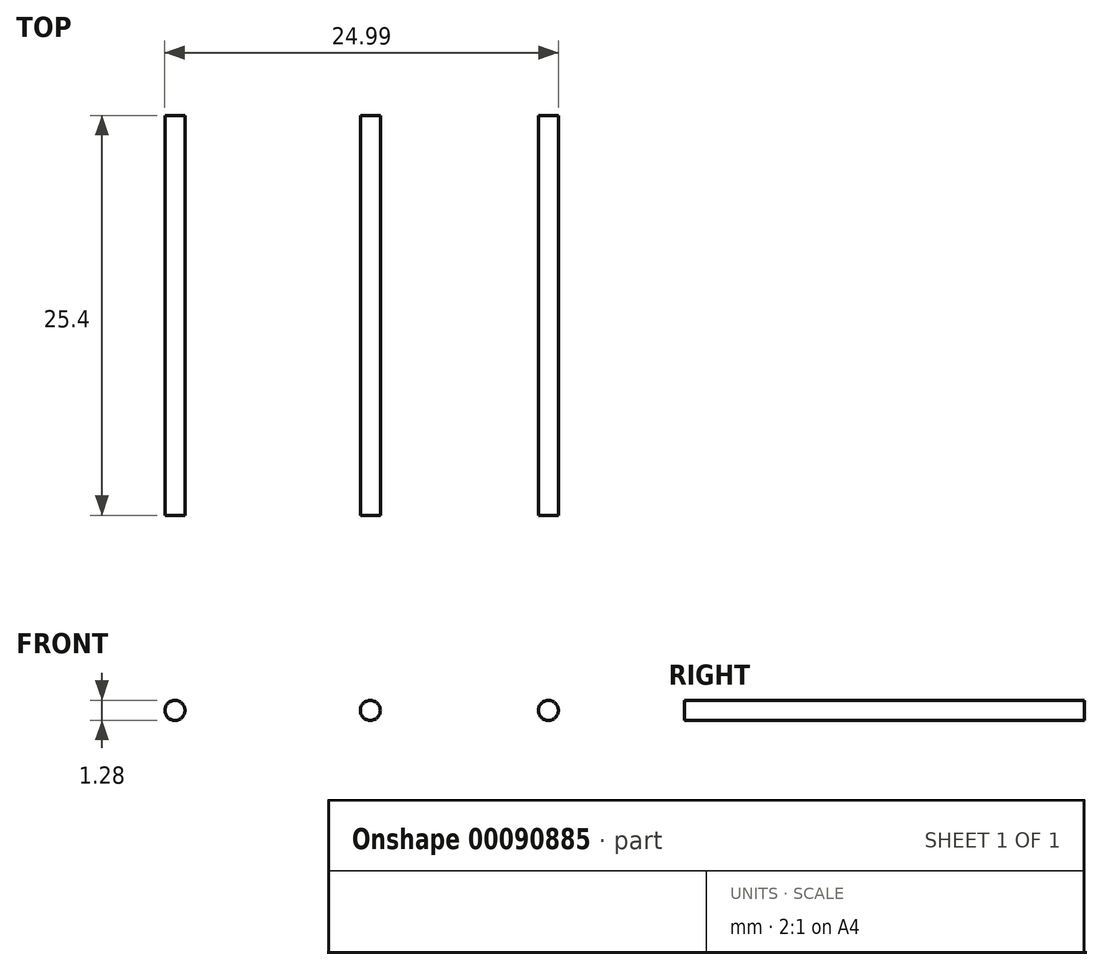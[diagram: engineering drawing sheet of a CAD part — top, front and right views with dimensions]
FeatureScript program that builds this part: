
annotation { "Feature Type Name" : "Feature", "Feature Type Description" : "" }
export const myFeature = defineFeature(function(context is Context, id is Id, definition is map)
    precondition{}
    {
        {
            var Q0;
            Q0=qCreatedBy(makeId("Front.planeOp"),FACE);
            var sketch = newSketch(context, id + "F0", { "sketchPlane" : qUnion([Q0])});
            skCircle(sketch, "E0", {"center": v(-13.07, 0) * mm, "radius": 0.64 * mm});
            skCircle(sketch, "E1", {"center": v(-0.66, 0) * mm, "radius": 0.64 * mm});
            skCircle(sketch, "E2", {"center": v(10.65, 0) * mm, "radius": 0.64 * mm});
            skSolve(sketch);
        }
        {
            var Q0;
            Q0=makeQuery(id+"F0.imprint","IMPRINT",FACE,{"disambiguationData":[TD([[makeQuery(id+"F0.imprint","IMPRINT",EDGE,{"derivedFrom":sQuery(id+"F0.wireOp",EDGE,"E1")}),1.0]])]});
            var Q1;
            Q1=makeQuery(id+"F0.imprint","IMPRINT",FACE,{"disambiguationData":[TD([[makeQuery(id+"F0.imprint","IMPRINT",EDGE,{"derivedFrom":sQuery(id+"F0.wireOp",EDGE,"E2")}),1.0]])]});
            var Q2;
            Q2=makeQuery(id+"F0.imprint","IMPRINT",FACE,{"disambiguationData":[TD([[makeQuery(id+"F0.imprint","IMPRINT",EDGE,{"derivedFrom":sQuery(id+"F0.wireOp",EDGE,"E0")}),1.0]])]});
            extrude(context, id + "F1", {"entities" : qUnion([Q0, Q1, Q2]), "depth" : 25.4 * mm});
        }
    });
